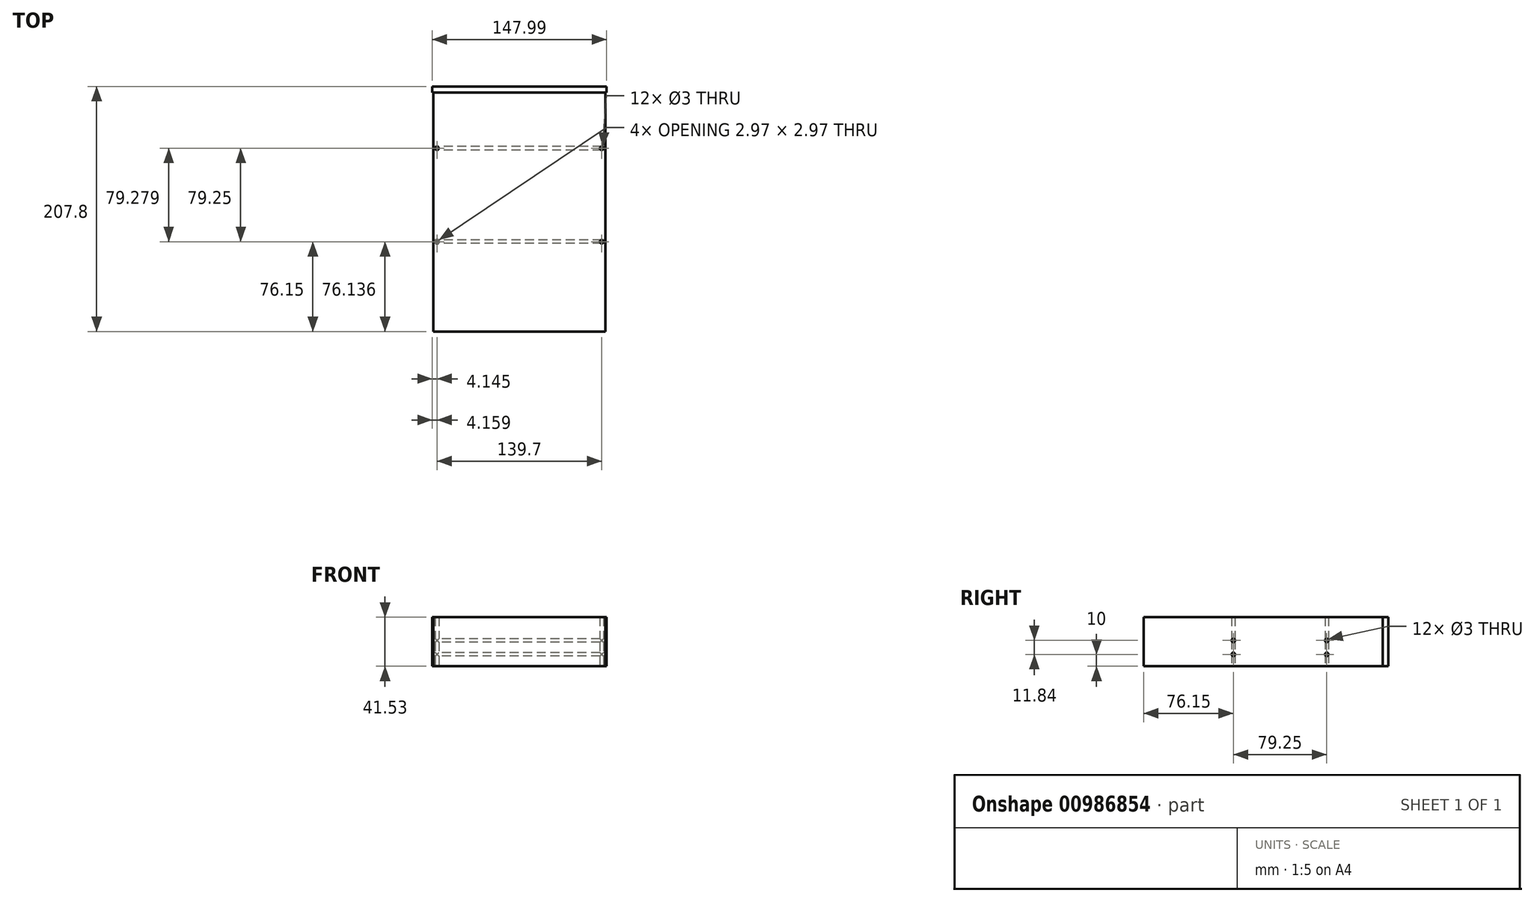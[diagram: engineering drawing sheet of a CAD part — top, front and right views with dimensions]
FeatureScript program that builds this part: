
annotation { "Feature Type Name" : "Feature", "Feature Type Description" : "" }
export const myFeature = defineFeature(function(context is Context, id is Id, definition is map)
    precondition{}
    {
        {
            var Q0;
            Q0=qCreatedBy(makeId("Top.planeOp"),FACE);
            var sketch = newSketch(context, id + "F0", { "sketchPlane" : qUnion([Q0])});
            skLineSegment(sketch, "E0.bottom", {"start": v(0, 0) * mm, "end": v(146.05, 0) * mm});
            skLineSegment(sketch, "E0.top", {"start": v(0, 202.8) * mm, "end": v(146.05, 202.8) * mm});
            skLineSegment(sketch, "E0.left", {"start": v(0, 0) * mm, "end": v(0, 202.8) * mm});
            skLineSegment(sketch, "E0.right", {"start": v(146.05, 0) * mm, "end": v(146.05, 202.8) * mm});
            skCircle(sketch, "E1", {"center": v(3.18, 155.4) * mm, "radius": 1.5 * mm});
            skCircle(sketch, "E2", {"center": v(3.18, 76.15) * mm, "radius": 1.5 * mm});
            skCircle(sketch, "E3", {"center": v(142.88, 76.15) * mm, "radius": 1.5 * mm});
            skCircle(sketch, "E4", {"center": v(142.88, 155.4) * mm, "radius": 1.5 * mm});
            skLineSegment(sketch, "E5.bottom", {"start": v(-0.98, 202.8) * mm, "end": v(147.02, 202.8) * mm});
            skLineSegment(sketch, "E5.top", {"start": v(-0.98, 207.8) * mm, "end": v(147.02, 207.8) * mm});
            skLineSegment(sketch, "E5.left", {"start": v(-0.98, 202.8) * mm, "end": v(-0.98, 207.8) * mm});
            skLineSegment(sketch, "E5.right", {"start": v(147.02, 202.8) * mm, "end": v(147.02, 207.8) * mm});
            skLineSegment(sketch, "E6", {"start": v(-0.98, 202.8) * mm, "end": v(0, 202.8) * mm, "construction": true});
            skLineSegment(sketch, "E7", {"start": v(146.05, 202.8) * mm, "end": v(147.02, 202.8) * mm, "construction": true});
            skLineSegment(sketch, "E8", {"start": v(3.18, 76.15) * mm, "end": v(0, 76.15) * mm, "construction": true});
            skLineSegment(sketch, "E9", {"start": v(142.88, 76.15) * mm, "end": v(146.05, 76.15) * mm, "construction": true});
            skSolve(sketch);
        }
        {
            var Q0;
            Q0=qCreatedBy(makeId("Right.planeOp"),FACE);
            var sketch = newSketch(context, id + "F1", { "sketchPlane" : qUnion([Q0])});
            skPoint(sketch, "E10.0", {"position": v(207.8, 0) * mm});
            skPoint(sketch, "E11.0", {"position": v(202.8, 0) * mm});
            skPoint(sketch, "E12.0", {"position": v(76.15, 0) * mm});
            skPoint(sketch, "E13.0", {"position": v(155.4, 0) * mm});
            skLineSegment(sketch, "E14.bottom", {"start": v(207.8, -0.38) * mm, "end": v(202.8, -0.38) * mm});
            skLineSegment(sketch, "E14.top", {"start": v(207.8, 41.91) * mm, "end": v(202.8, 41.91) * mm});
            skLineSegment(sketch, "E14.left", {"start": v(207.8, -0.38) * mm, "end": v(207.8, 41.91) * mm});
            skLineSegment(sketch, "E14.right", {"start": v(202.8, -0.38) * mm, "end": v(202.8, 41.91) * mm});
            skLineSegment(sketch, "E15.bottom", {"start": v(202.8, 0) * mm, "end": v(0, 0) * mm});
            skLineSegment(sketch, "E15.top", {"start": v(202.8, 41.53) * mm, "end": v(0, 41.53) * mm});
            skLineSegment(sketch, "E15.left", {"start": v(202.8, 0) * mm, "end": v(202.8, 41.53) * mm});
            skLineSegment(sketch, "E15.right", {"start": v(0, 0) * mm, "end": v(0, 41.53) * mm});
            skLineSegment(sketch, "E16", {"start": v(202.8, -0.38) * mm, "end": v(202.8, 0) * mm, "construction": true});
            skLineSegment(sketch, "E17", {"start": v(202.8, 41.53) * mm, "end": v(202.8, 41.91) * mm, "construction": true});
            skCircle(sketch, "E18", {"center": v(155.4, 10) * mm, "radius": 1.5 * mm});
            skCircle(sketch, "E19", {"center": v(155.4, 21.84) * mm, "radius": 1.5 * mm});
            skCircle(sketch, "E20", {"center": v(76.15, 21.84) * mm, "radius": 1.5 * mm});
            skCircle(sketch, "E21", {"center": v(76.15, 10) * mm, "radius": 1.5 * mm});
            skSolve(sketch);
        }
        {
            var Q0;
            Q0=makeQuery(id+"F0.imprint","IMPRINT",FACE,{"disambiguationData":[TD([[makeQuery(id+"F0.imprint","IMPRINT",EDGE,{"derivedFrom":sQuery(id+"F0.wireOp",EDGE,"E0.bottom")}),1.0]])]});
            var Q1;
            Q1=sQuery(id+"F1.wireOp",VERTEX,"E15.top.end");
            extrude(context, id + "F2", {"entities" : qUnion([Q0]), "endBound" : BoundingType.UP_TO_VERTEX, "depth" : 25 * mm, "endBoundEntityVertex" : qUnion([Q1]), "offsetDistance" : 25 * mm});
        }
        {
            var Q0;
            Q0=makeQuery(id+"F0.imprint","IMPRINT",FACE,{"disambiguationData":[TD([[makeQuery(id+"F0.imprint","IMPRINT",EDGE,{"derivedFrom":sQuery(id+"F0.wireOp",EDGE,"E5.top")}),-1.0]])]});
            var Q1;
            Q1=makeQuery(id+"F2.opExtrude","CAP_VERTEX",VERTEX,{"disambiguationData":[OSD([sQuery(id+"F0.wireOp",EDGE,"E0.right"),sQuery(id+"F0.wireOp",EDGE,"E5.bottom")])],"isStart":false});
            extrude(context, id + "F3", {"entities" : qUnion([Q0]), "endBound" : BoundingType.UP_TO_VERTEX, "depth" : 25 * mm, "endBoundEntityVertex" : qUnion([Q1]), "offsetDistance" : 25 * mm});
        }
        {
            var Q0;
            Q0=makeQuery(id+"F1.imprint","IMPRINT",FACE,{"disambiguationData":[TD([[makeQuery(id+"F1.imprint","IMPRINT",EDGE,{"derivedFrom":sQuery(id+"F1.wireOp",EDGE,"E19")}),1.0]])]});
            var Q1;
            Q1=makeQuery(id+"F1.imprint","IMPRINT",FACE,{"disambiguationData":[TD([[makeQuery(id+"F1.imprint","IMPRINT",EDGE,{"derivedFrom":sQuery(id+"F1.wireOp",EDGE,"E18")}),1.0]])]});
            var Q2;
            Q2=makeQuery(id+"F1.imprint","IMPRINT",FACE,{"disambiguationData":[TD([[makeQuery(id+"F1.imprint","IMPRINT",EDGE,{"derivedFrom":sQuery(id+"F1.wireOp",EDGE,"E20")}),1.0]])]});
            var Q3;
            Q3=makeQuery(id+"F1.imprint","IMPRINT",FACE,{"disambiguationData":[TD([[makeQuery(id+"F1.imprint","IMPRINT",EDGE,{"derivedFrom":sQuery(id+"F1.wireOp",EDGE,"E21")}),1.0]])]});
            extrude(context, id + "F4", {"entities" : qUnion([Q0, Q1, Q2, Q3]), "operationType" : NewBodyOperationType.REMOVE, "endBound" : BoundingType.THROUGH_ALL, "depth" : 25 * mm, "offsetDistance" : 25 * mm});
        }
    });
